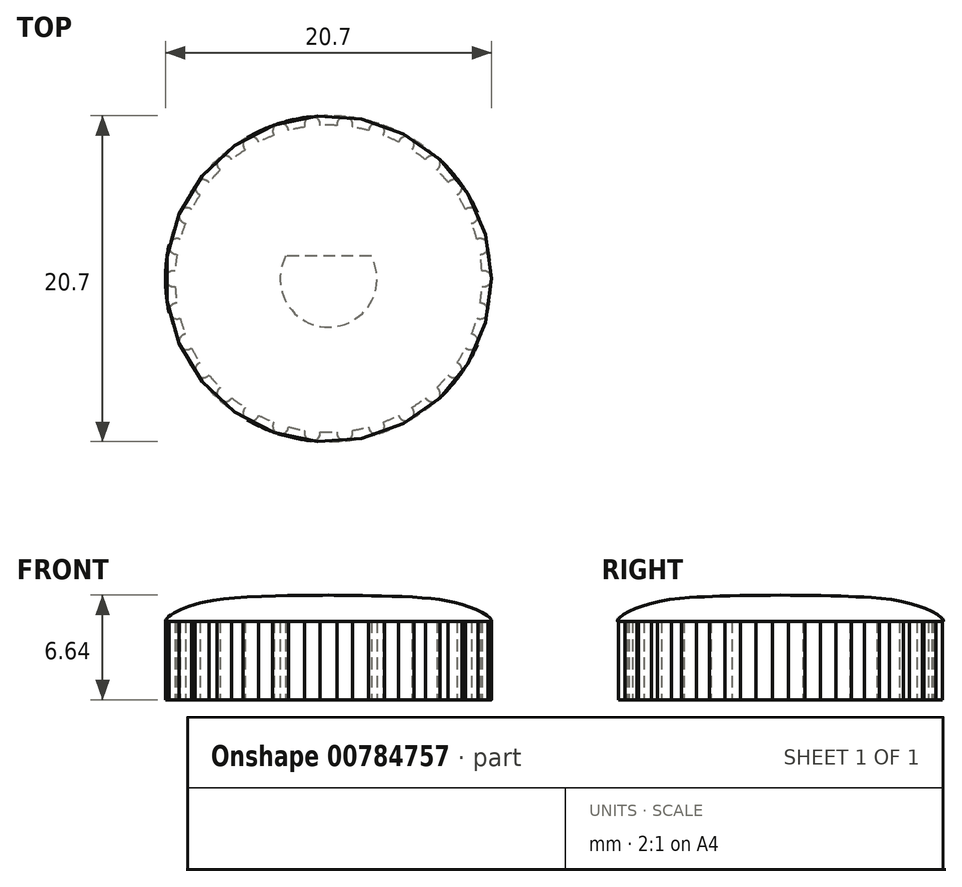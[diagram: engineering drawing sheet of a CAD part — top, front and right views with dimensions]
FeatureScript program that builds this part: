
annotation { "Feature Type Name" : "Feature", "Feature Type Description" : "" }
export const myFeature = defineFeature(function(context is Context, id is Id, definition is map)
    precondition{}
    {
        {
            var Q0;
            Q0=qCreatedBy(makeId("Top.planeOp"),FACE);
            var sketch = newSketch(context, id + "F0", { "sketchPlane" : qUnion([Q0])});
            skArc(sketch, "E0", {"start": v(-2.72, 1.44) * mm, "mid": v(0, -3.08) * mm, "end": v(2.72, 1.44) * mm});
            skArc(sketch, "E1", {"start": v(-9.74, -0.49) * mm, "mid": v(-9.7, -1.02) * mm, "end": v(-9.63, -1.55) * mm});
            skArc(sketch, "E2", {"start": v(-9.74, 0.49) * mm, "mid": v(-10.35, 0) * mm, "end": v(-9.74, -0.49) * mm});
            skArc(sketch, "E3.1.0", {"start": v(-9.63, -1.55) * mm, "mid": v(-10.12, -2.15) * mm, "end": v(-9.42, -2.5) * mm});
            skArc(sketch, "E3.2.0", {"start": v(-9.1, -3.52) * mm, "mid": v(-9.46, -4.21) * mm, "end": v(-8.7, -4.4) * mm});
            skArc(sketch, "E3.3.0", {"start": v(-8.16, -5.33) * mm, "mid": v(-8.37, -6.08) * mm, "end": v(-7.6, -6.12) * mm});
            skArc(sketch, "E3.4.0", {"start": v(-6.88, -6.91) * mm, "mid": v(-6.93, -7.7) * mm, "end": v(-6.15, -7.56) * mm});
            skArc(sketch, "E3.5.0", {"start": v(-5.3, -8.19) * mm, "mid": v(-5.18, -8.96) * mm, "end": v(-4.45, -8.68) * mm});
            skArc(sketch, "E3.6.0", {"start": v(-3.47, -9.11) * mm, "mid": v(-3.2, -9.84) * mm, "end": v(-2.55, -9.41) * mm});
            skArc(sketch, "E3.7.0", {"start": v(-1.5, -9.63) * mm, "mid": v(-1.08, -10.3) * mm, "end": v(-0.53, -9.74) * mm});
            skArc(sketch, "E3.8.0", {"start": v(0.53, -9.74) * mm, "mid": v(1.08, -10.3) * mm, "end": v(1.5, -9.63) * mm});
            skArc(sketch, "E3.9.0", {"start": v(2.55, -9.41) * mm, "mid": v(3.2, -9.84) * mm, "end": v(3.47, -9.11) * mm});
            skArc(sketch, "E3.10.0", {"start": v(4.45, -8.68) * mm, "mid": v(5.18, -8.96) * mm, "end": v(5.3, -8.19) * mm});
            skArc(sketch, "E3.11.0", {"start": v(6.15, -7.56) * mm, "mid": v(6.93, -7.7) * mm, "end": v(6.88, -6.91) * mm});
            skArc(sketch, "E3.12.0", {"start": v(7.6, -6.12) * mm, "mid": v(8.37, -6.08) * mm, "end": v(8.16, -5.33) * mm});
            skArc(sketch, "E3.13.0", {"start": v(8.7, -4.4) * mm, "mid": v(9.46, -4.21) * mm, "end": v(9.1, -3.52) * mm});
            skArc(sketch, "E3.14.0", {"start": v(9.42, -2.5) * mm, "mid": v(10.12, -2.15) * mm, "end": v(9.63, -1.55) * mm});
            skArc(sketch, "E3.15.0", {"start": v(9.74, -0.49) * mm, "mid": v(10.35, 0) * mm, "end": v(9.74, 0.49) * mm});
            skArc(sketch, "E3.16.0", {"start": v(9.63, 1.55) * mm, "mid": v(10.12, 2.15) * mm, "end": v(9.42, 2.5) * mm});
            skArc(sketch, "E3.17.0", {"start": v(9.1, 3.52) * mm, "mid": v(9.46, 4.21) * mm, "end": v(8.7, 4.4) * mm});
            skArc(sketch, "E3.18.0", {"start": v(8.16, 5.33) * mm, "mid": v(8.37, 6.08) * mm, "end": v(7.6, 6.12) * mm});
            skArc(sketch, "E3.19.0", {"start": v(6.88, 6.91) * mm, "mid": v(6.93, 7.7) * mm, "end": v(6.15, 7.56) * mm});
            skArc(sketch, "E3.20.0", {"start": v(5.3, 8.19) * mm, "mid": v(5.18, 8.96) * mm, "end": v(4.45, 8.68) * mm});
            skArc(sketch, "E3.21.0", {"start": v(3.47, 9.11) * mm, "mid": v(3.2, 9.84) * mm, "end": v(2.55, 9.41) * mm});
            skArc(sketch, "E3.22.0", {"start": v(1.5, 9.63) * mm, "mid": v(1.08, 10.3) * mm, "end": v(0.53, 9.74) * mm});
            skArc(sketch, "E3.23.0", {"start": v(-0.53, 9.74) * mm, "mid": v(-1.08, 10.3) * mm, "end": v(-1.5, 9.63) * mm});
            skArc(sketch, "E3.24.0", {"start": v(-2.55, 9.41) * mm, "mid": v(-3.2, 9.84) * mm, "end": v(-3.47, 9.11) * mm});
            skArc(sketch, "E3.25.0", {"start": v(-4.45, 8.68) * mm, "mid": v(-5.18, 8.96) * mm, "end": v(-5.3, 8.19) * mm});
            skArc(sketch, "E3.26.0", {"start": v(-6.15, 7.56) * mm, "mid": v(-6.93, 7.7) * mm, "end": v(-6.88, 6.91) * mm});
            skArc(sketch, "E3.27.0", {"start": v(-7.6, 6.12) * mm, "mid": v(-8.37, 6.08) * mm, "end": v(-8.16, 5.33) * mm});
            skArc(sketch, "E3.28.0", {"start": v(-8.7, 4.4) * mm, "mid": v(-9.46, 4.21) * mm, "end": v(-9.1, 3.52) * mm});
            skArc(sketch, "E3.29.0", {"start": v(-9.42, 2.5) * mm, "mid": v(-10.12, 2.15) * mm, "end": v(-9.63, 1.55) * mm});
            skArc(sketch, "E4.trimOffspring", {"start": v(-9.63, 1.55) * mm, "mid": v(-9.7, 1.02) * mm, "end": v(-9.74, 0.49) * mm});
            skArc(sketch, "E5.trimOffspring", {"start": v(-9.1, 3.52) * mm, "mid": v(-9.27, 3.01) * mm, "end": v(-9.42, 2.5) * mm});
            skArc(sketch, "E6.trimOffspring", {"start": v(-8.16, 5.33) * mm, "mid": v(-8.44, 4.88) * mm, "end": v(-8.7, 4.4) * mm});
            skArc(sketch, "E7.trimOffspring", {"start": v(-6.88, 6.91) * mm, "mid": v(-7.25, 6.52) * mm, "end": v(-7.6, 6.12) * mm});
            skArc(sketch, "E8.trimOffspring", {"start": v(-5.3, 8.19) * mm, "mid": v(-5.73, 7.89) * mm, "end": v(-6.15, 7.56) * mm});
            skArc(sketch, "E9.trimOffspring", {"start": v(-3.47, 9.11) * mm, "mid": v(-3.97, 8.9) * mm, "end": v(-4.45, 8.68) * mm});
            skArc(sketch, "E10.trimOffspring", {"start": v(-1.5, 9.63) * mm, "mid": v(-2.03, 9.54) * mm, "end": v(-2.55, 9.41) * mm});
            skArc(sketch, "E11.trimOffspring", {"start": v(0.53, 9.74) * mm, "mid": v(0, 9.75) * mm, "end": v(-0.53, 9.74) * mm});
            skArc(sketch, "E12.trimOffspring", {"start": v(2.55, 9.41) * mm, "mid": v(2.03, 9.54) * mm, "end": v(1.5, 9.63) * mm});
            skArc(sketch, "E13.trimOffspring", {"start": v(4.45, 8.68) * mm, "mid": v(3.97, 8.9) * mm, "end": v(3.47, 9.11) * mm});
            skArc(sketch, "E14.trimOffspring", {"start": v(6.15, 7.56) * mm, "mid": v(5.73, 7.89) * mm, "end": v(5.3, 8.19) * mm});
            skArc(sketch, "E15.trimOffspring", {"start": v(7.6, 6.12) * mm, "mid": v(7.25, 6.52) * mm, "end": v(6.88, 6.91) * mm});
            skArc(sketch, "E16.trimOffspring", {"start": v(8.7, 4.4) * mm, "mid": v(8.44, 4.87) * mm, "end": v(8.16, 5.33) * mm});
            skArc(sketch, "E17.trimOffspring", {"start": v(9.42, 2.5) * mm, "mid": v(9.27, 3.01) * mm, "end": v(9.1, 3.52) * mm});
            skArc(sketch, "E18.trimOffspring", {"start": v(9.74, 0.49) * mm, "mid": v(9.7, 1.02) * mm, "end": v(9.63, 1.55) * mm});
            skArc(sketch, "E19.trimOffspring", {"start": v(9.63, -1.55) * mm, "mid": v(9.7, -1.02) * mm, "end": v(9.74, -0.49) * mm});
            skArc(sketch, "E20.trimOffspring", {"start": v(8.16, -5.33) * mm, "mid": v(8.44, -4.87) * mm, "end": v(8.7, -4.4) * mm});
            skArc(sketch, "E21.trimOffspring", {"start": v(6.88, -6.91) * mm, "mid": v(7.25, -6.52) * mm, "end": v(7.6, -6.12) * mm});
            skArc(sketch, "E22.trimOffspring", {"start": v(5.3, -8.19) * mm, "mid": v(5.73, -7.89) * mm, "end": v(6.15, -7.56) * mm});
            skArc(sketch, "E23.trimOffspring", {"start": v(3.47, -9.11) * mm, "mid": v(3.97, -8.9) * mm, "end": v(4.45, -8.68) * mm});
            skArc(sketch, "E24.trimOffspring", {"start": v(1.5, -9.63) * mm, "mid": v(2.03, -9.54) * mm, "end": v(2.55, -9.41) * mm});
            skArc(sketch, "E25.trimOffspring", {"start": v(-0.53, -9.74) * mm, "mid": v(0, -9.75) * mm, "end": v(0.53, -9.74) * mm});
            skArc(sketch, "E26.trimOffspring", {"start": v(-2.55, -9.41) * mm, "mid": v(-2.03, -9.54) * mm, "end": v(-1.5, -9.63) * mm});
            skArc(sketch, "E27.trimOffspring", {"start": v(-4.45, -8.68) * mm, "mid": v(-3.97, -8.9) * mm, "end": v(-3.47, -9.11) * mm});
            skArc(sketch, "E28.trimOffspring", {"start": v(-6.15, -7.56) * mm, "mid": v(-5.73, -7.89) * mm, "end": v(-5.3, -8.19) * mm});
            skArc(sketch, "E29.trimOffspring", {"start": v(-7.6, -6.12) * mm, "mid": v(-7.25, -6.52) * mm, "end": v(-6.88, -6.91) * mm});
            skArc(sketch, "E30.trimOffspring", {"start": v(-8.7, -4.4) * mm, "mid": v(-8.44, -4.88) * mm, "end": v(-8.16, -5.33) * mm});
            skArc(sketch, "E31.trimOffspring", {"start": v(-9.42, -2.5) * mm, "mid": v(-9.27, -3.01) * mm, "end": v(-9.1, -3.52) * mm});
            skArc(sketch, "E32.trimOffspring", {"start": v(9.1, -3.52) * mm, "mid": v(9.27, -3.01) * mm, "end": v(9.42, -2.5) * mm});
            skLineSegment(sketch, "E33", {"start": v(2.72, 1.44) * mm, "end": v(-2.72, 1.44) * mm});
            skSolve(sketch);
        }
        {
            var Q0;
            Q0=makeQuery(id+"F0.imprint","IMPRINT",FACE,{"disambiguationData":[TD([[makeQuery(id+"F0.imprint","IMPRINT",EDGE,{"derivedFrom":sQuery(id+"F0.wireOp",EDGE,"E0")}),-1.0]])]});
            extrude(context, id + "F1", {"entities" : qUnion([Q0]), "depth" : 5 * mm, "offsetDistance" : 25 * mm});
        }
        {
            var Q0;
            Q0=qCreatedBy(makeId("Front.planeOp"),FACE);
            var sketch = newSketch(context, id + "F2", { "sketchPlane" : qUnion([Q0])});
            skLineSegment(sketch, "E34", {"start": v(0, 4.98) * mm, "end": v(10.35, 4.98) * mm});
            skFitSpline(sketch, "E35", {"points": [v(10.35, 4.98) * mm, v(10.35, 5.02) * mm, v(10.16, 5.27) * mm, v(8.56, 6.02) * mm, v(5.83, 6.48) * mm, v(1.77, 6.62) * mm, v(0, 6.64) * mm], "startDerivative": vector(0.21, 1.3) * mm, "endDerivative": vector(-8.24, 0.06) * mm});
            skLineSegment(sketch, "E36", {"start": v(0, 6.64) * mm, "end": v(0, 4.98) * mm});
            skSolve(sketch);
        }
        {
            var Q0;
            Q0 = qSketchRegion(id + "F2", true);
            var Q1;
            Q1=sQuery(id+"F2.wireOp",EDGE,"E36");
            revolve(context, id + "F3", {"operationType" : NewBodyOperationType.ADD, "surfaceOperationType" : NewSurfaceOperationType.NEW, "entities" : qUnion([Q0]), "axis" : qUnion([Q1]), "revolveType" : RevolveType.FULL});
        }
    });
